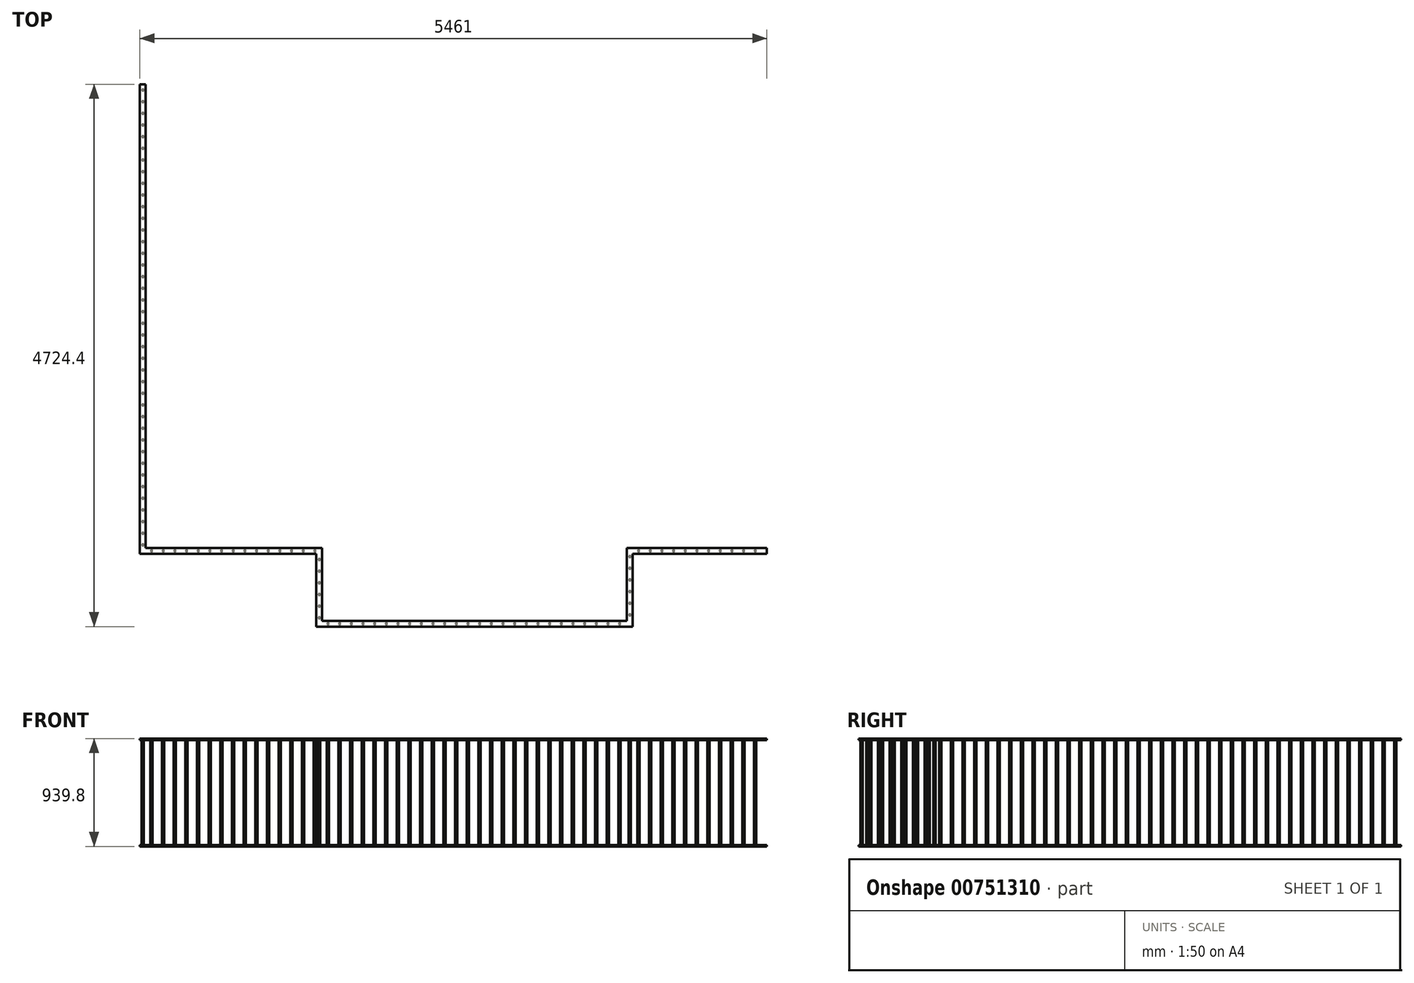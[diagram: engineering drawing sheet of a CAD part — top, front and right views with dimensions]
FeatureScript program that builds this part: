
annotation { "Feature Type Name" : "Feature", "Feature Type Description" : "" }
export const myFeature = defineFeature(function(context is Context, id is Id, definition is map)
    precondition{}
    {
        {
            var Q0;
            Q0=qCreatedBy(makeId("Top.planeOp"),FACE);
            var sketch = newSketch(context, id + "F0", { "sketchPlane" : qUnion([Q0])});
            skLineSegment(sketch, "E0.bottom", {"start": v(0, 0) * mm, "end": v(50.8, 0) * mm});
            skLineSegment(sketch, "E0.top", {"start": v(0, -4089.4) * mm, "end": v(50.8, -4089.4) * mm});
            skLineSegment(sketch, "E0.left", {"start": v(0, 0) * mm, "end": v(0, -4089.4) * mm});
            skLineSegment(sketch, "E0.right", {"start": v(50.8, 0) * mm, "end": v(50.8, -4038.6) * mm});
            skLineSegment(sketch, "E1.bottom", {"start": v(50.8, -4089.4) * mm, "end": v(1536.7, -4089.4) * mm});
            skLineSegment(sketch, "E1.top", {"start": v(50.8, -4038.6) * mm, "end": v(1536.7, -4038.6) * mm});
            skLineSegment(sketch, "E1.right", {"start": v(1536.7, -4089.4) * mm, "end": v(1536.7, -4038.6) * mm});
            skLineSegment(sketch, "E2.bottom", {"start": v(1536.7, -4038.6) * mm, "end": v(1587.5, -4038.6) * mm});
            skLineSegment(sketch, "E2.top", {"start": v(1536.7, -4673.6) * mm, "end": v(1587.5, -4673.6) * mm});
            skLineSegment(sketch, "E2.left", {"start": v(1536.7, -4038.6) * mm, "end": v(1536.7, -4673.6) * mm});
            skLineSegment(sketch, "E2.right", {"start": v(1587.5, -4038.6) * mm, "end": v(1587.5, -4673.6) * mm});
            skLineSegment(sketch, "E3.bottom", {"start": v(1536.7, -4673.6) * mm, "end": v(4241.8, -4673.6) * mm});
            skLineSegment(sketch, "E3.top", {"start": v(1536.7, -4724.4) * mm, "end": v(4241.8, -4724.4) * mm});
            skLineSegment(sketch, "E3.left", {"start": v(1536.7, -4673.6) * mm, "end": v(1536.7, -4724.4) * mm});
            skLineSegment(sketch, "E3.right", {"start": v(4241.8, -4673.6) * mm, "end": v(4241.8, -4724.4) * mm});
            skLineSegment(sketch, "E4.bottom", {"start": v(4241.8, -4724.4) * mm, "end": v(4292.6, -4724.4) * mm});
            skLineSegment(sketch, "E4.top", {"start": v(4241.8, -4089.4) * mm, "end": v(4292.6, -4089.4) * mm});
            skLineSegment(sketch, "E4.left", {"start": v(4241.8, -4724.4) * mm, "end": v(4241.8, -4089.4) * mm});
            skLineSegment(sketch, "E4.right", {"start": v(4292.6, -4724.4) * mm, "end": v(4292.6, -4089.4) * mm});
            skLineSegment(sketch, "E5.bottom", {"start": v(4241.8, -4089.4) * mm, "end": v(5461, -4089.4) * mm});
            skLineSegment(sketch, "E5.top", {"start": v(4241.8, -4038.6) * mm, "end": v(5461, -4038.6) * mm});
            skLineSegment(sketch, "E5.left", {"start": v(4241.8, -4089.4) * mm, "end": v(4241.8, -4038.6) * mm});
            skLineSegment(sketch, "E5.right", {"start": v(5461, -4089.4) * mm, "end": v(5461, -4038.6) * mm});
            skSolve(sketch);
        }
        {
            var Q0;
            Q0 = qSketchRegion(id + "F0", true);
            extrude(context, id + "F1", {"entities" : qUnion([Q0]), "depth" : 12.7 * mm, "offsetDistance" : 25.4 * mm});
        }
        {
            var Q0;
            Q0=makeQuery(id+"F1.opExtrude","CAP_FACE",FACE,{"disambiguationData":[OSD([sQuery(id+"F0.wireOp",EDGE,"E0.bottom"),sQuery(id+"F0.wireOp",EDGE,"E0.top"),sQuery(id+"F0.wireOp",EDGE,"E0.left"),sQuery(id+"F0.wireOp",EDGE,"E0.right"),sQuery(id+"F0.wireOp",EDGE,"E1.bottom"),sQuery(id+"F0.wireOp",EDGE,"E1.top"),sQuery(id+"F0.wireOp",EDGE,"E2.bottom"),sQuery(id+"F0.wireOp",EDGE,"E2.left"),sQuery(id+"F0.wireOp",EDGE,"E2.right"),sQuery(id+"F0.wireOp",EDGE,"E3.bottom"),sQuery(id+"F0.wireOp",EDGE,"E3.top"),sQuery(id+"F0.wireOp",EDGE,"E3.left"),sQuery(id+"F0.wireOp",EDGE,"E4.bottom"),sQuery(id+"F0.wireOp",EDGE,"E4.left"),sQuery(id+"F0.wireOp",EDGE,"E4.right"),sQuery(id+"F0.wireOp",EDGE,"E5.bottom"),sQuery(id+"F0.wireOp",EDGE,"E5.top"),sQuery(id+"F0.wireOp",EDGE,"E5.left"),sQuery(id+"F0.wireOp",EDGE,"E5.right")])],"isStart":false});
            var sketch = newSketch(context, id + "F2", { "sketchPlane" : qUnion([Q0])});
            skCircle(sketch, "E6", {"center": v(25.4, -50.8) * mm, "radius": 9.53 * mm});
            skPoint(sketch, "E6.centerSnap0", {"position": v(25.4, 0) * mm});
            skCircle(sketch, "E7.0.1.0", {"center": v(25.4, -152.4) * mm, "radius": 9.53 * mm});
            skCircle(sketch, "E7.0.2.0", {"center": v(25.4, -254) * mm, "radius": 9.53 * mm});
            skCircle(sketch, "E7.0.3.0", {"center": v(25.4, -355.6) * mm, "radius": 9.53 * mm});
            skCircle(sketch, "E7.0.4.0", {"center": v(25.4, -457.2) * mm, "radius": 9.53 * mm});
            skCircle(sketch, "E7.0.5.0", {"center": v(25.4, -558.8) * mm, "radius": 9.53 * mm});
            skCircle(sketch, "E7.0.6.0", {"center": v(25.4, -660.4) * mm, "radius": 9.53 * mm});
            skCircle(sketch, "E7.0.7.0", {"center": v(25.4, -762) * mm, "radius": 9.53 * mm});
            skCircle(sketch, "E7.0.8.0", {"center": v(25.4, -863.6) * mm, "radius": 9.53 * mm});
            skCircle(sketch, "E7.0.9.0", {"center": v(25.4, -965.2) * mm, "radius": 9.53 * mm});
            skCircle(sketch, "E7.0.10.0", {"center": v(25.4, -1066.8) * mm, "radius": 9.53 * mm});
            skCircle(sketch, "E7.0.11.0", {"center": v(25.4, -1168.4) * mm, "radius": 9.53 * mm});
            skCircle(sketch, "E7.0.12.0", {"center": v(25.4, -1270) * mm, "radius": 9.53 * mm});
            skCircle(sketch, "E7.0.13.0", {"center": v(25.4, -1371.6) * mm, "radius": 9.53 * mm});
            skCircle(sketch, "E7.0.14.0", {"center": v(25.4, -1473.2) * mm, "radius": 9.53 * mm});
            skCircle(sketch, "E7.0.15.0", {"center": v(25.4, -1574.8) * mm, "radius": 9.53 * mm});
            skCircle(sketch, "E7.0.16.0", {"center": v(25.4, -1676.4) * mm, "radius": 9.53 * mm});
            skCircle(sketch, "E7.0.17.0", {"center": v(25.4, -1778) * mm, "radius": 9.53 * mm});
            skCircle(sketch, "E7.0.18.0", {"center": v(25.4, -1879.6) * mm, "radius": 9.53 * mm});
            skCircle(sketch, "E7.0.19.0", {"center": v(25.4, -1981.2) * mm, "radius": 9.53 * mm});
            skCircle(sketch, "E7.0.20.0", {"center": v(25.4, -2082.8) * mm, "radius": 9.53 * mm});
            skCircle(sketch, "E7.0.21.0", {"center": v(25.4, -2184.4) * mm, "radius": 9.53 * mm});
            skCircle(sketch, "E7.0.22.0", {"center": v(25.4, -2286) * mm, "radius": 9.53 * mm});
            skCircle(sketch, "E7.0.23.0", {"center": v(25.4, -2387.6) * mm, "radius": 9.53 * mm});
            skCircle(sketch, "E7.0.24.0", {"center": v(25.4, -2489.2) * mm, "radius": 9.53 * mm});
            skCircle(sketch, "E7.0.25.0", {"center": v(25.4, -2590.8) * mm, "radius": 9.53 * mm});
            skCircle(sketch, "E7.0.26.0", {"center": v(25.4, -2692.4) * mm, "radius": 9.53 * mm});
            skCircle(sketch, "E7.0.27.0", {"center": v(25.4, -2794) * mm, "radius": 9.53 * mm});
            skCircle(sketch, "E7.0.28.0", {"center": v(25.4, -2895.6) * mm, "radius": 9.53 * mm});
            skCircle(sketch, "E7.0.29.0", {"center": v(25.4, -2997.2) * mm, "radius": 9.53 * mm});
            skCircle(sketch, "E7.0.30.0", {"center": v(25.4, -3098.8) * mm, "radius": 9.53 * mm});
            skCircle(sketch, "E7.0.31.0", {"center": v(25.4, -3200.4) * mm, "radius": 9.53 * mm});
            skCircle(sketch, "E7.0.32.0", {"center": v(25.4, -3302) * mm, "radius": 9.53 * mm});
            skCircle(sketch, "E7.0.33.0", {"center": v(25.4, -3403.6) * mm, "radius": 9.53 * mm});
            skCircle(sketch, "E7.0.34.0", {"center": v(25.4, -3505.2) * mm, "radius": 9.53 * mm});
            skCircle(sketch, "E7.0.35.0", {"center": v(25.4, -3606.8) * mm, "radius": 9.53 * mm});
            skCircle(sketch, "E7.0.36.0", {"center": v(25.4, -3708.4) * mm, "radius": 9.53 * mm});
            skCircle(sketch, "E7.0.37.0", {"center": v(25.4, -3810) * mm, "radius": 9.53 * mm});
            skCircle(sketch, "E7.0.38.0", {"center": v(25.4, -3911.6) * mm, "radius": 9.53 * mm});
            skCircle(sketch, "E7.0.39.0", {"center": v(25.4, -4013.2) * mm, "radius": 9.53 * mm});
            skLineSegment(sketch, "E7.direction1", {"start": v(25.4, -50.8) * mm, "end": v(50.8, -50.8) * mm, "construction": true});
            skLineSegment(sketch, "E7.direction2", {"start": v(25.4, -50.8) * mm, "end": v(25.4, -152.4) * mm, "construction": true});
            skCircle(sketch, "E8", {"center": v(101.6, -4064) * mm, "radius": 9.53 * mm});
            skCircle(sketch, "E9.1.0.0", {"center": v(203.2, -4064) * mm, "radius": 9.53 * mm});
            skCircle(sketch, "E9.2.0.0", {"center": v(304.8, -4064) * mm, "radius": 9.53 * mm});
            skCircle(sketch, "E9.3.0.0", {"center": v(406.4, -4064) * mm, "radius": 9.53 * mm});
            skCircle(sketch, "E9.4.0.0", {"center": v(508, -4064) * mm, "radius": 9.53 * mm});
            skCircle(sketch, "E9.5.0.0", {"center": v(609.6, -4064) * mm, "radius": 9.53 * mm});
            skCircle(sketch, "E9.6.0.0", {"center": v(711.2, -4064) * mm, "radius": 9.53 * mm});
            skCircle(sketch, "E9.7.0.0", {"center": v(812.8, -4064) * mm, "radius": 9.53 * mm});
            skCircle(sketch, "E9.8.0.0", {"center": v(914.4, -4064) * mm, "radius": 9.53 * mm});
            skCircle(sketch, "E9.9.0.0", {"center": v(1016, -4064) * mm, "radius": 9.53 * mm});
            skCircle(sketch, "E9.10.0.0", {"center": v(1117.6, -4064) * mm, "radius": 9.53 * mm});
            skCircle(sketch, "E9.11.0.0", {"center": v(1219.2, -4064) * mm, "radius": 9.53 * mm});
            skCircle(sketch, "E9.12.0.0", {"center": v(1320.8, -4064) * mm, "radius": 9.53 * mm});
            skCircle(sketch, "E9.13.0.0", {"center": v(1422.4, -4064) * mm, "radius": 9.53 * mm});
            skCircle(sketch, "E9.14.0.0", {"center": v(1524, -4064) * mm, "radius": 9.53 * mm});
            skLineSegment(sketch, "E9.direction1", {"start": v(101.6, -4064) * mm, "end": v(203.2, -4064) * mm, "construction": true});
            skCircle(sketch, "E10", {"center": v(1562.1, -4140.2) * mm, "radius": 9.53 * mm});
            skCircle(sketch, "E11.0.1.0", {"center": v(1562.1, -4241.8) * mm, "radius": 9.53 * mm});
            skCircle(sketch, "E11.0.2.0", {"center": v(1562.1, -4343.4) * mm, "radius": 9.53 * mm});
            skCircle(sketch, "E11.0.3.0", {"center": v(1562.1, -4445) * mm, "radius": 9.53 * mm});
            skCircle(sketch, "E11.0.4.0", {"center": v(1562.1, -4546.6) * mm, "radius": 9.53 * mm});
            skCircle(sketch, "E11.0.5.0", {"center": v(1562.1, -4648.2) * mm, "radius": 9.53 * mm});
            skLineSegment(sketch, "E11.direction1", {"start": v(1562.1, -4140.2) * mm, "end": v(1587.5, -4140.2) * mm, "construction": true});
            skLineSegment(sketch, "E11.direction2", {"start": v(1562.1, -4140.2) * mm, "end": v(1562.1, -4241.8) * mm, "construction": true});
            skCircle(sketch, "E12", {"center": v(1638.3, -4699) * mm, "radius": 9.53 * mm});
            skCircle(sketch, "E13.1.0.0", {"center": v(1739.9, -4699) * mm, "radius": 9.53 * mm});
            skCircle(sketch, "E13.2.0.0", {"center": v(1841.5, -4699) * mm, "radius": 9.53 * mm});
            skCircle(sketch, "E13.3.0.0", {"center": v(1943.1, -4699) * mm, "radius": 9.53 * mm});
            skCircle(sketch, "E13.4.0.0", {"center": v(2044.7, -4699) * mm, "radius": 9.53 * mm});
            skCircle(sketch, "E13.5.0.0", {"center": v(2146.3, -4699) * mm, "radius": 9.53 * mm});
            skCircle(sketch, "E13.6.0.0", {"center": v(2247.9, -4699) * mm, "radius": 9.53 * mm});
            skCircle(sketch, "E13.7.0.0", {"center": v(2349.5, -4699) * mm, "radius": 9.53 * mm});
            skCircle(sketch, "E13.8.0.0", {"center": v(2451.1, -4699) * mm, "radius": 9.53 * mm});
            skCircle(sketch, "E13.9.0.0", {"center": v(2552.7, -4699) * mm, "radius": 9.53 * mm});
            skCircle(sketch, "E13.10.0.0", {"center": v(2654.3, -4699) * mm, "radius": 9.53 * mm});
            skCircle(sketch, "E13.11.0.0", {"center": v(2755.9, -4699) * mm, "radius": 9.53 * mm});
            skCircle(sketch, "E13.12.0.0", {"center": v(2857.5, -4699) * mm, "radius": 9.53 * mm});
            skCircle(sketch, "E13.13.0.0", {"center": v(2959.1, -4699) * mm, "radius": 9.53 * mm});
            skCircle(sketch, "E13.14.0.0", {"center": v(3060.7, -4699) * mm, "radius": 9.53 * mm});
            skCircle(sketch, "E13.15.0.0", {"center": v(3162.3, -4699) * mm, "radius": 9.53 * mm});
            skCircle(sketch, "E13.16.0.0", {"center": v(3263.9, -4699) * mm, "radius": 9.53 * mm});
            skCircle(sketch, "E13.17.0.0", {"center": v(3365.5, -4699) * mm, "radius": 9.53 * mm});
            skCircle(sketch, "E13.18.0.0", {"center": v(3467.1, -4699) * mm, "radius": 9.53 * mm});
            skCircle(sketch, "E13.19.0.0", {"center": v(3568.7, -4699) * mm, "radius": 9.53 * mm});
            skCircle(sketch, "E13.20.0.0", {"center": v(3670.3, -4699) * mm, "radius": 9.53 * mm});
            skCircle(sketch, "E13.21.0.0", {"center": v(3771.9, -4699) * mm, "radius": 9.53 * mm});
            skCircle(sketch, "E13.22.0.0", {"center": v(3873.5, -4699) * mm, "radius": 9.53 * mm});
            skCircle(sketch, "E13.23.0.0", {"center": v(3975.1, -4699) * mm, "radius": 9.53 * mm});
            skCircle(sketch, "E13.24.0.0", {"center": v(4076.7, -4699) * mm, "radius": 9.53 * mm});
            skCircle(sketch, "E13.25.0.0", {"center": v(4178.3, -4699) * mm, "radius": 9.53 * mm});
            skLineSegment(sketch, "E13.direction1", {"start": v(1638.3, -4699) * mm, "end": v(1739.9, -4699) * mm, "construction": true});
            skCircle(sketch, "E14", {"center": v(4267.2, -4622.8) * mm, "radius": 9.53 * mm});
            skCircle(sketch, "E15.0.1.0", {"center": v(4267.2, -4521.2) * mm, "radius": 9.53 * mm});
            skCircle(sketch, "E15.0.2.0", {"center": v(4267.2, -4419.6) * mm, "radius": 9.53 * mm});
            skCircle(sketch, "E15.0.3.0", {"center": v(4267.2, -4318) * mm, "radius": 9.53 * mm});
            skCircle(sketch, "E15.0.4.0", {"center": v(4267.2, -4216.4) * mm, "radius": 9.53 * mm});
            skLineSegment(sketch, "E15.direction1", {"start": v(4267.2, -4622.8) * mm, "end": v(4292.6, -4622.8) * mm, "construction": true});
            skLineSegment(sketch, "E15.direction2", {"start": v(4267.2, -4622.8) * mm, "end": v(4267.2, -4521.2) * mm, "construction": true});
            skCircle(sketch, "E16.0.0.5", {"center": v(4267.2, -4114.8) * mm, "radius": 9.53 * mm});
            skCircle(sketch, "E17", {"center": v(4343.4, -4064) * mm, "radius": 9.53 * mm});
            skCircle(sketch, "E18.1.0.0", {"center": v(4445, -4064) * mm, "radius": 9.53 * mm});
            skCircle(sketch, "E18.2.0.0", {"center": v(4546.6, -4064) * mm, "radius": 9.53 * mm});
            skCircle(sketch, "E18.3.0.0", {"center": v(4648.2, -4064) * mm, "radius": 9.53 * mm});
            skCircle(sketch, "E18.4.0.0", {"center": v(4749.8, -4064) * mm, "radius": 9.53 * mm});
            skCircle(sketch, "E18.5.0.0", {"center": v(4851.4, -4064) * mm, "radius": 9.53 * mm});
            skCircle(sketch, "E18.6.0.0", {"center": v(4953, -4064) * mm, "radius": 9.53 * mm});
            skCircle(sketch, "E18.7.0.0", {"center": v(5054.6, -4064) * mm, "radius": 9.53 * mm});
            skCircle(sketch, "E18.8.0.0", {"center": v(5156.2, -4064) * mm, "radius": 9.53 * mm});
            skCircle(sketch, "E18.9.0.0", {"center": v(5257.8, -4064) * mm, "radius": 9.53 * mm});
            skCircle(sketch, "E18.10.0.0", {"center": v(5359.4, -4064) * mm, "radius": 9.53 * mm});
            skLineSegment(sketch, "E18.direction1", {"start": v(4343.4, -4064) * mm, "end": v(4445, -4064) * mm, "construction": true});
            skSolve(sketch);
        }
        {
            var Q0;
            Q0 = qSketchRegion(id + "F2", true);
            extrude(context, id + "F3", {"entities" : qUnion([Q0]), "operationType" : NewBodyOperationType.ADD, "depth" : 914.4 * mm, "offsetDistance" : 25.4 * mm});
        }
        {
            var Q0;
            Q0=makeQuery(id+"F3.opExtrude","CAP_FACE",FACE,{"disambiguationData":[OSD([sQuery(id+"F2.wireOp",EDGE,"E6")])],"isStart":false});
            var sketch = newSketch(context, id + "F4", { "sketchPlane" : qUnion([Q0])});
            skLineSegment(sketch, "E19.0", {"start": v(0, 0) * mm, "end": v(50.8, 0) * mm});
            skLineSegment(sketch, "E19.1", {"start": v(0, -4089.4) * mm, "end": v(50.8, -4089.4) * mm});
            skLineSegment(sketch, "E19.2", {"start": v(0, 0) * mm, "end": v(0, -4089.4) * mm});
            skLineSegment(sketch, "E19.3", {"start": v(50.8, 0) * mm, "end": v(50.8, -4038.6) * mm});
            skLineSegment(sketch, "E19.4", {"start": v(50.8, -4089.4) * mm, "end": v(1536.7, -4089.4) * mm});
            skLineSegment(sketch, "E19.5", {"start": v(50.8, -4038.6) * mm, "end": v(1536.7, -4038.6) * mm});
            skLineSegment(sketch, "E19.6", {"start": v(1536.7, -4089.4) * mm, "end": v(1536.7, -4038.6) * mm});
            skLineSegment(sketch, "E19.7", {"start": v(1536.7, -4038.6) * mm, "end": v(1587.5, -4038.6) * mm});
            skLineSegment(sketch, "E19.8", {"start": v(1536.7, -4673.6) * mm, "end": v(1587.5, -4673.6) * mm});
            skLineSegment(sketch, "E19.9", {"start": v(1536.7, -4038.6) * mm, "end": v(1536.7, -4673.6) * mm});
            skLineSegment(sketch, "E19.10", {"start": v(1587.5, -4038.6) * mm, "end": v(1587.5, -4673.6) * mm});
            skLineSegment(sketch, "E19.11", {"start": v(1536.7, -4673.6) * mm, "end": v(4241.8, -4673.6) * mm});
            skLineSegment(sketch, "E19.12", {"start": v(1536.7, -4724.4) * mm, "end": v(4241.8, -4724.4) * mm});
            skLineSegment(sketch, "E19.13", {"start": v(1536.7, -4673.6) * mm, "end": v(1536.7, -4724.4) * mm});
            skLineSegment(sketch, "E19.14", {"start": v(4241.8, -4673.6) * mm, "end": v(4241.8, -4724.4) * mm});
            skLineSegment(sketch, "E19.15", {"start": v(4241.8, -4724.4) * mm, "end": v(4292.6, -4724.4) * mm});
            skLineSegment(sketch, "E19.16", {"start": v(4241.8, -4089.4) * mm, "end": v(4292.6, -4089.4) * mm});
            skLineSegment(sketch, "E19.17", {"start": v(4241.8, -4724.4) * mm, "end": v(4241.8, -4089.4) * mm});
            skLineSegment(sketch, "E19.18", {"start": v(4292.6, -4724.4) * mm, "end": v(4292.6, -4089.4) * mm});
            skLineSegment(sketch, "E19.19", {"start": v(4241.8, -4089.4) * mm, "end": v(5461, -4089.4) * mm});
            skLineSegment(sketch, "E19.20", {"start": v(4241.8, -4038.6) * mm, "end": v(5461, -4038.6) * mm});
            skLineSegment(sketch, "E19.21", {"start": v(4241.8, -4089.4) * mm, "end": v(4241.8, -4038.6) * mm});
            skLineSegment(sketch, "E19.22", {"start": v(5461, -4089.4) * mm, "end": v(5461, -4038.6) * mm});
            skSolve(sketch);
        }
        {
            var Q0;
            Q0 = qSketchRegion(id + "F4", true);
            extrude(context, id + "F5", {"entities" : qUnion([Q0]), "operationType" : NewBodyOperationType.ADD, "depth" : 12.7 * mm, "offsetDistance" : 25.4 * mm});
        }
    });
